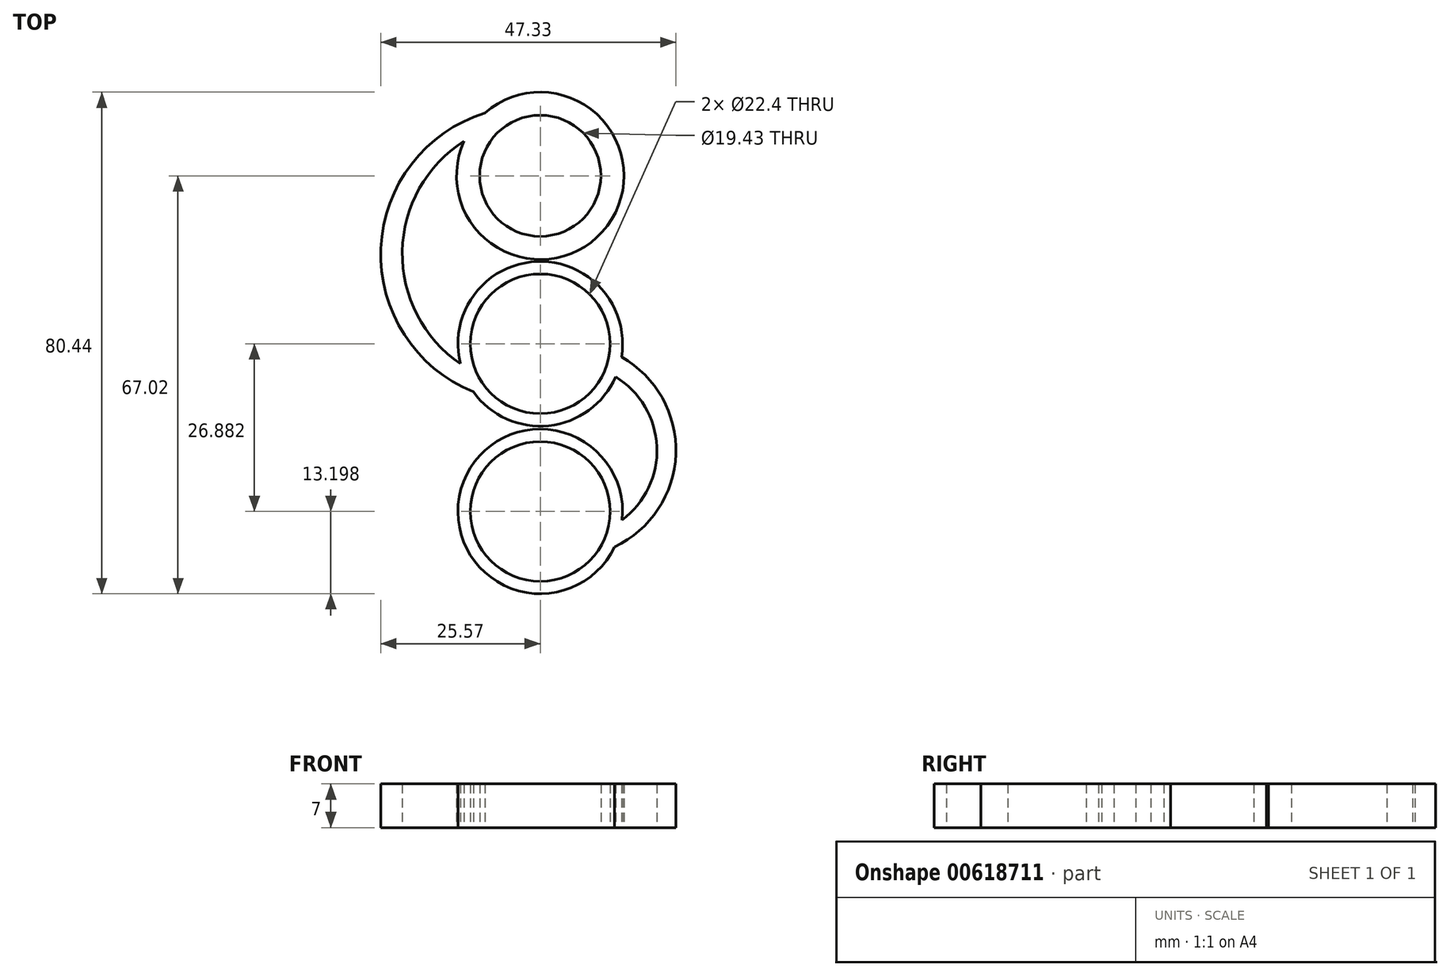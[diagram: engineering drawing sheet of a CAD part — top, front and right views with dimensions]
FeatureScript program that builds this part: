
annotation { "Feature Type Name" : "Feature", "Feature Type Description" : "" }
export const myFeature = defineFeature(function(context is Context, id is Id, definition is map)
    precondition{}
    {
        {
            var Q0;
            Q0=qCreatedBy(makeId("Top.planeOp"),FACE);
            var sketch = newSketch(context, id + "F0", { "sketchPlane" : qUnion([Q0])});
            skCircle(sketch, "E0", {"center": v(0, 0) * mm, "radius": 11.2 * mm});
            skCircle(sketch, "E1", {"center": v(0, 0) * mm, "radius": 13.2 * mm});
            skCircle(sketch, "E2", {"center": v(0, 26.94) * mm, "radius": 9.71 * mm});
            skCircle(sketch, "E3", {"center": v(0, 26.94) * mm, "radius": 13.42 * mm});
            skCircle(sketch, "E4", {"center": v(0, -26.88) * mm, "radius": 11.2 * mm});
            skCircle(sketch, "E5", {"center": v(0, -26.88) * mm, "radius": 13.2 * mm});
            skArc(sketch, "E6", {"start": v(-12.2, 32.52) * mm, "mid": v(-22.11, 14.82) * mm, "end": v(-12.8, -3.21) * mm});
            skArc(sketch, "E7", {"start": v(13.13, -28.26) * mm, "mid": v(18.7, -16.5) * mm, "end": v(12.1, -5.3) * mm});
            skArc(sketch, "E8", {"start": v(11.92, -32.56) * mm, "mid": v(21.74, -17.68) * mm, "end": v(13.03, -2.12) * mm});
            skArc(sketch, "E9", {"start": v(-8.85, 37.02) * mm, "mid": v(-25.55, 15.32) * mm, "end": v(-10.72, -7.7) * mm});
            skSolve(sketch);
        }
        {
            var Q0;
            Q0=makeQuery(id+"F0.imprint","IMPRINT",FACE,{"disambiguationData":[TD([[makeQuery(id+"F0.imprint","IMPRINT",EDGE,{"derivedFrom":sQuery(id+"F0.wireOp",EDGE,"E2")}),-1.0]])]});
            var Q1;
            Q1=makeQuery(id+"F0.imprint","IMPRINT",FACE,{"disambiguationData":[TD([[makeQuery(id+"F0.imprint","IMPRINT",EDGE,{"derivedFrom":sQuery(id+"F0.wireOp",EDGE,"E0")}),-1.0]])]});
            var Q2;
            {var subQ0=sQuery(id+"F0.wireOp",EDGE,"E7");Q2=makeQuery(id+"F0.imprint","IMPRINT",FACE,{"disambiguationData":[TD([[makeQuery(id+"F0.imprint","IMPRINT",EDGE,{"derivedFrom":subQ0}),-1.0]])]});}
            var Q3;
            Q3=makeQuery(id+"F0.imprint","IMPRINT",FACE,{"disambiguationData":[TD([[makeQuery(id+"F0.imprint","IMPRINT",EDGE,{"derivedFrom":sQuery(id+"F0.wireOp",EDGE,"E4")}),-1.0]])]});
            var Q4;
            {var subQ0=sQuery(id+"F0.wireOp",EDGE,"E6");Q4=makeQuery(id+"F0.imprint","IMPRINT",FACE,{"disambiguationData":[TD([[makeQuery(id+"F0.imprint","IMPRINT",EDGE,{"derivedFrom":subQ0}),-1.0]])]});}
            extrude(context, id + "F1", {"entities" : qUnion([Q0, Q1, Q2, Q3, Q4]), "depth" : 7 * mm, "offsetDistance" : 25 * mm});
        }
    });
